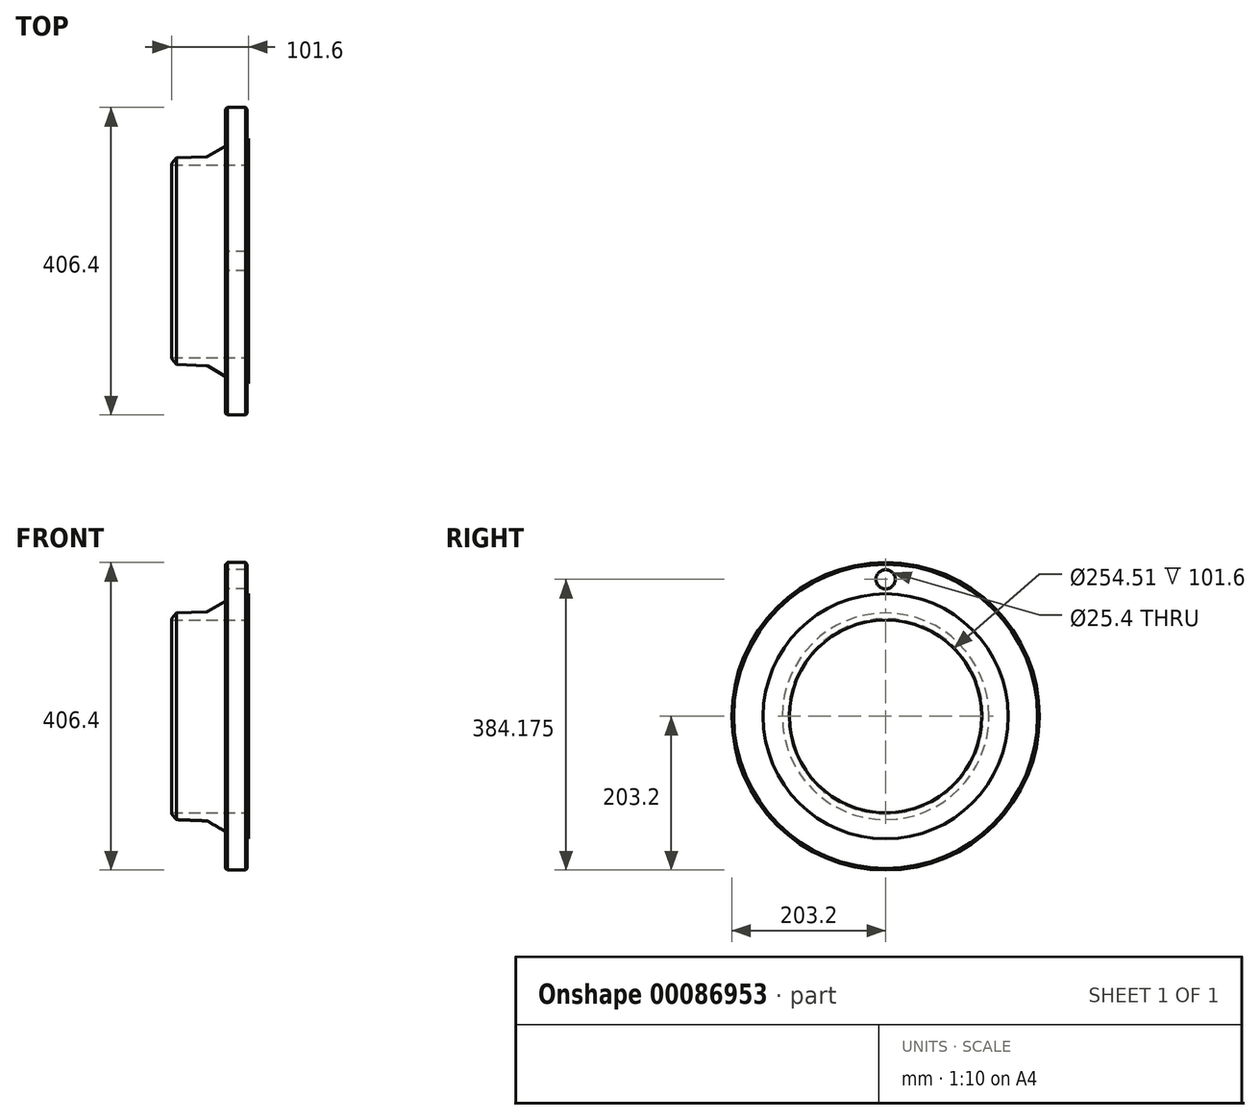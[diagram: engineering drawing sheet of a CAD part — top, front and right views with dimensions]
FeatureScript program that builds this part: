
annotation { "Feature Type Name" : "Feature", "Feature Type Description" : "" }
export const myFeature = defineFeature(function(context is Context, id is Id, definition is map)
    precondition{}
    {
        {
            var Q0;
            Q0=qCreatedBy(makeId("Front.planeOp"),FACE);
            var sketch = newSketch(context, id + "F0", { "sketchPlane" : qUnion([Q0])});
            skLineSegment(sketch, "E0", {"start": v(0, 0) * mm, "end": v(0, 0) * mm});
            skLineSegment(sketch, "E1", {"start": v(0, 0) * mm, "end": v(-142.76, 0) * mm, "construction": true});
            skLineSegment(sketch, "E2", {"start": v(0, 0) * mm, "end": v(0, 127.25) * mm, "construction": true});
            skLineSegment(sketch, "E3", {"start": v(0, 127.25) * mm, "end": v(0, 161.93) * mm});
            skLineSegment(sketch, "E4", {"start": v(0, 161.93) * mm, "end": v(-1.59, 161.93) * mm});
            skLineSegment(sketch, "E5", {"start": v(-1.59, 161.93) * mm, "end": v(-1.59, 203.2) * mm});
            skLineSegment(sketch, "E6", {"start": v(-1.59, 203.2) * mm, "end": v(-30.16, 203.2) * mm});
            skLineSegment(sketch, "E7", {"start": v(-30.16, 203.2) * mm, "end": v(-30.16, 152.4) * mm});
            skLineSegment(sketch, "E8", {"start": v(-30.16, 152.4) * mm, "end": v(-54.61, 138.11) * mm});
            skLineSegment(sketch, "E9", {"start": v(-54.61, 138.11) * mm, "end": v(-95.25, 136.53) * mm});
            skLineSegment(sketch, "E10", {"start": v(-95.25, 136.52) * mm, "end": v(-101.6, 128.84) * mm});
            skLineSegment(sketch, "E11", {"start": v(-101.6, 128.84) * mm, "end": v(-101.6, 127.25) * mm});
            skLineSegment(sketch, "E12", {"start": v(-101.6, 127.25) * mm, "end": v(0, 127.25) * mm});
            skSolve(sketch);
        }
        {
            var Q0;
            Q0 = qSketchRegion(id + "F0", true);
            var Q1;
            Q1=sQuery(id+"F0.wireOp",EDGE,"E1");
            revolve(context, id + "F1", {"entities" : qUnion([Q0]), "axis" : qUnion([Q1]), "revolveType" : RevolveType.FULL});
        }
        {
            var Q0;
            Q0=makeQuery(id+"F1.opRevolve","SWEPT_FACE",FACE,{"disambiguationData":[OSD([sQuery(id+"F0.wireOp",EDGE,"E7")])]});
            var sketch = newSketch(context, id + "F2", { "sketchPlane" : qUnion([Q0])});
            skLineSegment(sketch, "E13", {"start": v(0, 0) * mm, "end": v(0, 180.98) * mm, "construction": true});
            skCircle(sketch, "E14", {"center": v(0, 180.98) * mm, "radius": 12.7 * mm});
            skSolve(sketch);
        }
        {
            var Q0;
            Q0 = qSketchRegion(id + "F2", true);
            extrude(context, id + "F3", {"entities" : qUnion([Q0]), "operationType" : NewBodyOperationType.REMOVE, "endBound" : BoundingType.THROUGH_ALL, "oppositeDirection" : true, "depth" : 25.4 * mm});
        }
        {
            var Q0;
            Q0=makeQuery(id+"F1.opRevolve","SWEPT_EDGE",EDGE,{"disambiguationData":[OSD([sQuery(id+"F0.wireOp",EDGE,"E7"),sQuery(id+"F0.wireOp",EDGE,"E8")])]});
            var Q1;
            Q1=makeQuery(id+"F1.opRevolve","SWEPT_EDGE",EDGE,{"disambiguationData":[OSD([sQuery(id+"F0.wireOp",EDGE,"E8"),sQuery(id+"F0.wireOp",EDGE,"E9")])]});
            fillet(context, id + "F4", {"entities" : qUnion([Q0, Q1]), "radius" : 3.17 * mm, "tangentPropagation" : true, "allowEdgeOverflow" : false});
        }
        {
            var Q0;
            Q0=makeQuery(id+"F1.opRevolve","SWEPT_FACE",FACE,{"disambiguationData":[OSD([sQuery(id+"F0.wireOp",EDGE,"E6")])]});
            chamfer(context, id + "F5", {"entities" : qUnion([Q0]), "chamferType" : ChamferType.OFFSET_ANGLE, "width" : 2.3 * mm, "oppositeDirection" : false, "angle" : 45 * degree, "tangentPropagation" : true});
        }
    });
